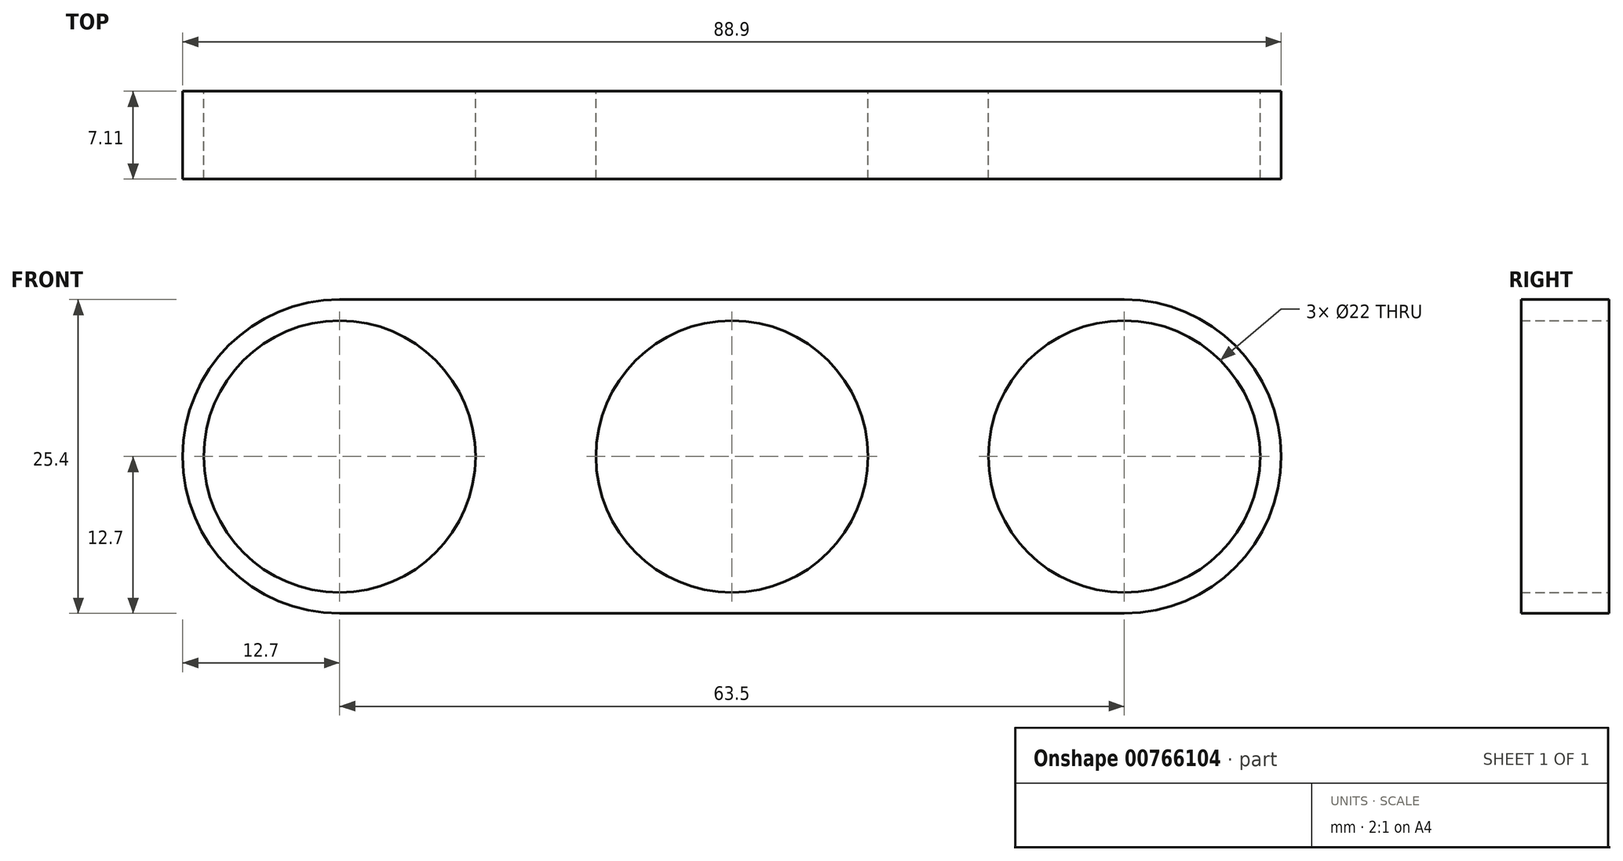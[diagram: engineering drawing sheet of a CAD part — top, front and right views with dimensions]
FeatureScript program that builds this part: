
annotation { "Feature Type Name" : "Feature", "Feature Type Description" : "" }
export const myFeature = defineFeature(function(context is Context, id is Id, definition is map)
    precondition{}
    {
        {
            var Q0;
            Q0=qCreatedBy(makeId("Front.planeOp"),FACE);
            var sketch = newSketch(context, id + "F0", { "sketchPlane" : qUnion([Q0])});
            skCircle(sketch, "E0", {"center": v(0, 0) * mm, "radius": 11 * mm});
            skCircle(sketch, "E1", {"center": v(31.75, 0) * mm, "radius": 11 * mm});
            skCircle(sketch, "E2", {"center": v(-31.75, 0) * mm, "radius": 11 * mm});
            skCircle(sketch, "E3", {"center": v(-31.75, 0) * mm, "radius": 12.7 * mm});
            skCircle(sketch, "E4", {"center": v(31.75, 0) * mm, "radius": 12.7 * mm});
            skLineSegment(sketch, "E5", {"start": v(-31.75, 12.7) * mm, "end": v(31.75, 12.7) * mm});
            skLineSegment(sketch, "E6", {"start": v(-31.75, -12.7) * mm, "end": v(31.75, -12.7) * mm});
            skPoint(sketch, "E7.start.orphan", {"position": v(0, -11) * mm});
            skPoint(sketch, "E8.start.orphan", {"position": v(0, 11) * mm});
            skSolve(sketch);
        }
        {
            var Q0;
            {var subQ4=sQuery(id+"F0.wireOp",EDGE,"E8");Q0=makeQuery(id+"F0.imprint","IMPRINT",FACE,{"disambiguationData":[TD([[makeQuery(id+"F0.imprint","IMPRINT",EDGE,{"derivedFrom":subQ4}),-1.0]])]});}
            var Q1;
            Q1=makeQuery(id+"F0.imprint","IMPRINT",FACE,{"disambiguationData":[TD([[makeQuery(id+"F0.imprint","IMPRINT",EDGE,{"derivedFrom":sQuery(id+"F0.wireOp",EDGE,"E1")}),-1.0]])]});
            var Q2;
            {var subQ4=sQuery(id+"F0.wireOp",EDGE,"E8");Q2=makeQuery(id+"F0.imprint","IMPRINT",FACE,{"disambiguationData":[TD([[makeQuery(id+"F0.imprint","IMPRINT",EDGE,{"derivedFrom":subQ4}),1.0]])]});}
            var Q3;
            Q3=makeQuery(id+"F0.imprint","IMPRINT",FACE,{"disambiguationData":[TD([[makeQuery(id+"F0.imprint","IMPRINT",EDGE,{"derivedFrom":sQuery(id+"F0.wireOp",EDGE,"E2")}),-1.0]])]});
            var Q4;
            Q4=makeQuery(id+"F0.imprint","IMPRINT",FACE,{"disambiguationData":[TD([[makeQuery(id+"F0.imprint","IMPRINT",EDGE,{"derivedFrom":sQuery(id+"F0.wireOp",EDGE,"E0")}),-1.0]])]});
            extrude(context, id + "F1", {"entities" : qUnion([Q0, Q1, Q2, Q3, Q4]), "depth" : 7.11 * mm, "offsetDistance" : 25.4 * mm});
        }
    });
